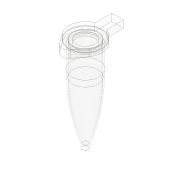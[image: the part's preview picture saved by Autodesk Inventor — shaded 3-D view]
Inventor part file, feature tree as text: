
AUTODESK INVENTOR PART (.ipt)
format: ipt  version: 2017 (Build 210142000, 142)  size: 205,312 bytes
history: native  units: in
note: dims shown in document units (in); Inventor stores cm internally (conversion verified against a paired STEP export)
features: sketch x5, extrude x3, revolve x2, projected_geometry x1
ambient origin geometry x8: Origin, YZ Plane, XZ Plane, XY Plane, X Axis, Y Axis, Z Axis, Center Point
bodies: Solid1 (feature_tree)
feature tree (11):
  revolve  "Revolution1"  [1 undecoded]
  extrude  "Extrusion1"  Depth=0.1063in
  revolve  "Revolution2"  [1 undecoded]
  extrude  "Extrusion2"  Depth=0.28in
  extrude  "Extrusion3"  Depth=0.275in
  sketch  "Sketch1"  dims[d0=0.1181in d1=0.6in]
  sketch  "Sketch2"  dims[d2=0.7874in d3=0.1063in]
  sketch  "Sketch3"  dims[d4=90.0deg d7=0.25in]
  sketch  "Sketch4"  dims[d8=0.0859in d9=0.28in]
  sketch  "Sketch5"  dims[d10=0.03in d11=0.0in d12=0.275in d13=0.029in d14=90.0deg d15=0.1in d16=0.198in d17=1.0in d18=0.0in d19=1.0in d20=0.0in]
  projected_geometry  "Projected Loop1"
note: 2 required parameter values undecoded (feature->parameter linkage not recoverable at this tier; creation-order binding heuristic only, values carry confidence <= 0.55)
